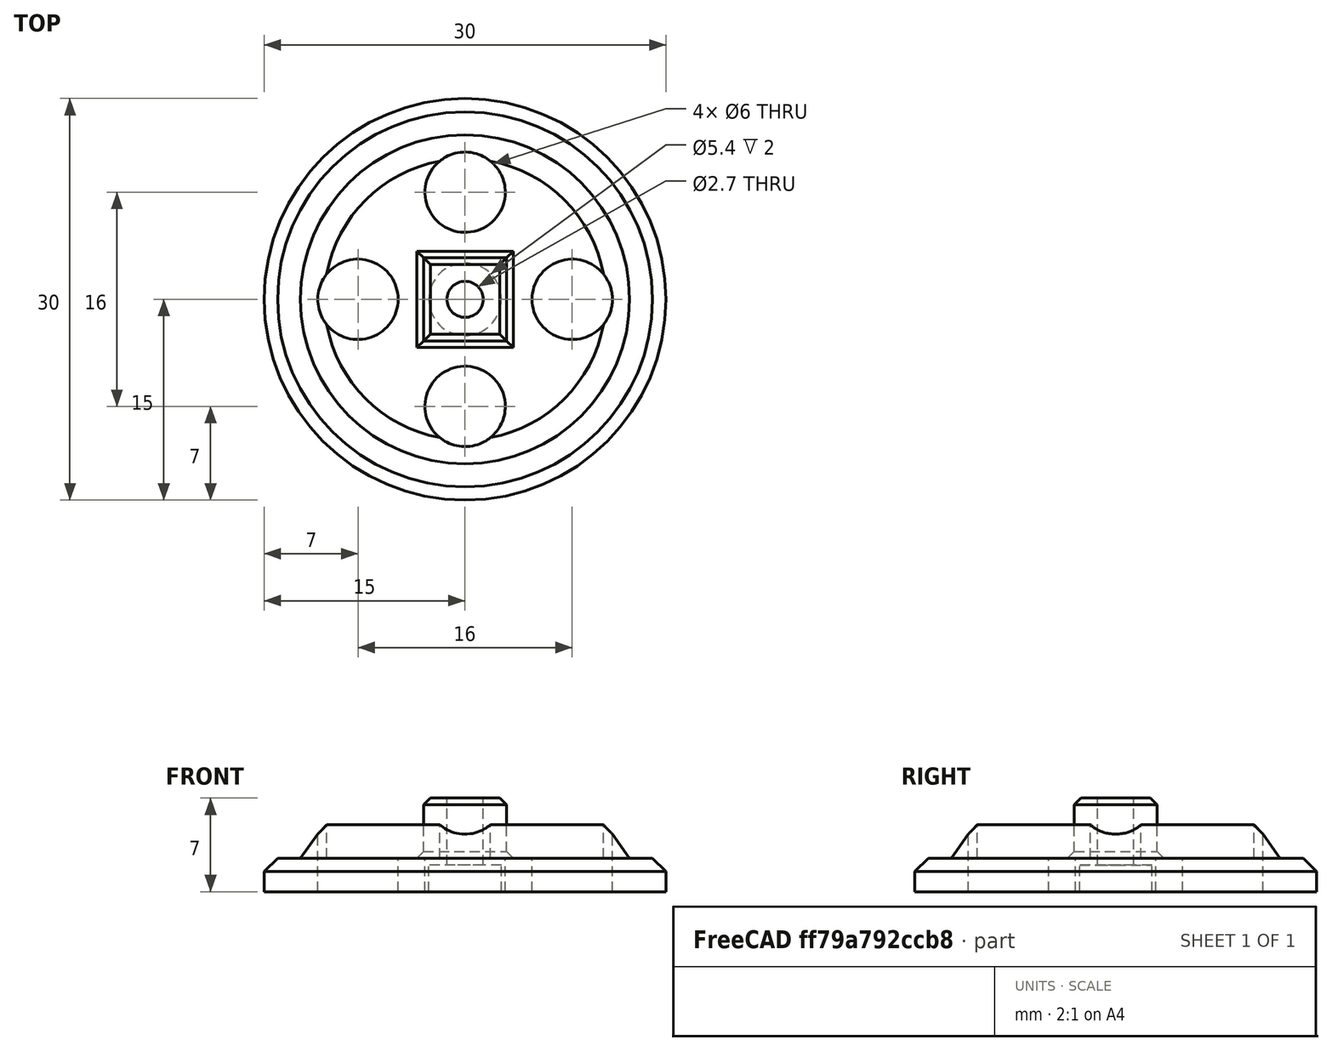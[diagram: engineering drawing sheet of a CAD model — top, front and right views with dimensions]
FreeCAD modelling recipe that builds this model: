
FCSTD DOCUMENT  (FreeCAD 0.15R4671 (Git))
Label: tendon_wheel_ax_fingers_top
License: CC-BY 3.0
LicenseURL: http://creativecommons.org/licenses/by/3.0/
objects: Part::Cylinder×8, Part::MultiFuse×4, Part::Cut×3, Part::Chamfer×3, Part::Cone×1, Part::Box×1
note: 20 computed .brp shape members not serialized (recipe doc carries the construction recipe); baked Part::Feature solids carry a one-line shape summary decoded from their .brp

FEATURE [Part::Cylinder] Cylinder
  Angle = 360
  Height = 6
  Placement = pos=(0,0,2) rot=(0,0,1;0rad)
  Radius = 10.5
FEATURE [Part::Cylinder] Cylinder001
  Angle = 360
  Height = 2.5
  Placement = pos=(0,0,-0.5) rot=(0,0,1;0rad)
  Radius = 15
FEATURE [Part::Cone] Cone
  Angle = 360
  Height = 3.5
  Placement = pos=(0,0,1) rot=(0,0,1;0rad)
  Radius1 = 13
  Radius2 = 10.5
FEATURE [Part::Box] Box  label="Cube"
  Height = 4.5
  Length = 6.2
  Placement = pos=(-3.1,-3.1,2) rot=(0,0,1;0rad)
  Width = 6.2
FEATURE [Part::MultiFuse] Fusion
  Shapes = -> [Cone,Cylinder001]
FEATURE [Part::Cylinder] Cylinder002  label="Cylinder004"
  Angle = 360
  Height = 20
  Placement = pos=(0,0,-5) rot=(0,0,1;0rad)
  Radius = 1.35
FEATURE [Part::Cut] Cut
  Base = -> Fusion
  Tool = -> Cylinder
FEATURE [Part::MultiFuse] Fusion001
  Shapes = -> [Cut,Box]
FEATURE [Part::Cylinder] Cylinder003  label="Cylinder012"
  Angle = 360
  Height = 2
  Placement = pos=(0,0,-0.5) rot=(0,0,1;0rad)
  Radius = 2.7
FEATURE [Part::MultiFuse] Fusion002
  Shapes = -> [Cylinder003,Cylinder002]
FEATURE [Part::Cut] Cut001
  Base = -> Fusion001
  Tool = -> Fusion002
FEATURE [Part::Chamfer] Chamfer
  Base = -> Cut001
  Edges = 4 edges r=0.5: [Edge1,Edge2,Edge3,Edge4]
FEATURE [Part::Cylinder] Cylinder005  label="TopHole005"
  Angle = 360
  Height = 20
  Placement = pos=(8,0,-4) rot=(0,0,1;0rad)
  Radius = 3
FEATURE [Part::Cylinder] Cylinder008  label="TopHole006"
  Angle = 360
  Height = 20
  Placement = pos=(0,8,-4) rot=(0,0,1;0rad)
  Radius = 3
FEATURE [Part::Cylinder] Cylinder009  label="TopHole004"
  Angle = 360
  Height = 20
  Placement = pos=(-8,0,-4) rot=(0,0,1;0rad)
  Radius = 3
FEATURE [Part::Cylinder] Cylinder011  label="TopHole007"
  Angle = 360
  Height = 20
  Placement = pos=(0,-8,-4) rot=(0,0,1;0rad)
  Radius = 3
FEATURE [Part::MultiFuse] Fusion003
  Shapes = -> [Cylinder011,Cylinder008,Cylinder009,Cylinder005]
FEATURE [Part::Cut] Cut002
  Base = -> Chamfer
  Tool = -> Fusion003
FEATURE [Part::Chamfer] Chamfer001
  Base = -> Cut002
  Edges = 4 edges r=0.5: [Edge17,Edge20,Edge22,Edge23]
FEATURE [Part::Chamfer] Chamfer002
  Base = -> Chamfer001
  Edges = 1 edges r=1: [Edge73]
